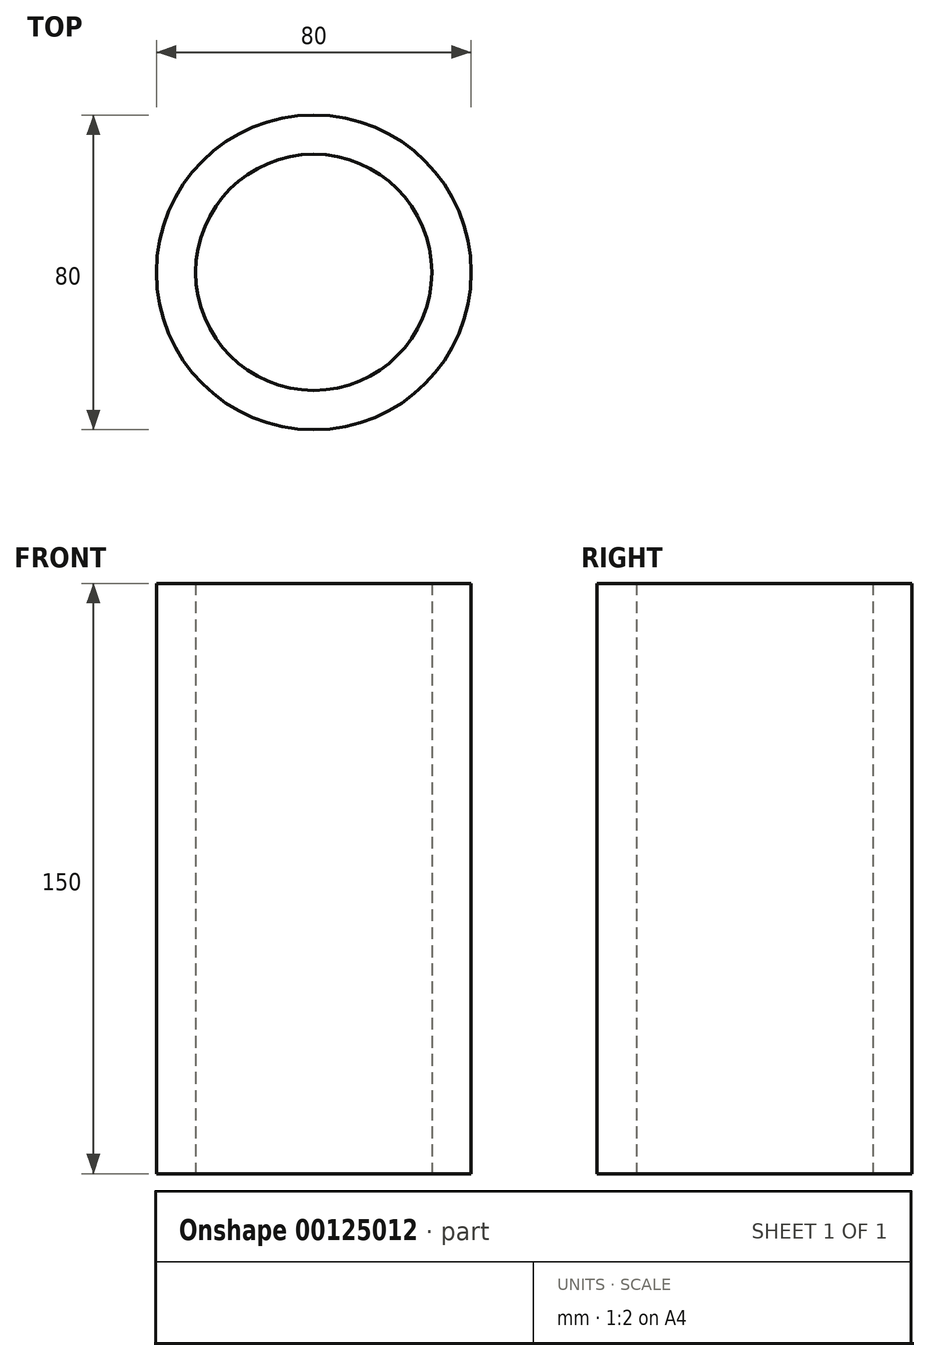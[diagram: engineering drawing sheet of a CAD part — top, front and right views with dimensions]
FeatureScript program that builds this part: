
annotation { "Feature Type Name" : "Feature", "Feature Type Description" : "" }
export const myFeature = defineFeature(function(context is Context, id is Id, definition is map)
    precondition{}
    {
        {
            var Q0;
            Q0=qCreatedBy(makeId("Top.planeOp"),FACE);
            var sketch = newSketch(context, id + "F0", { "sketchPlane" : qUnion([Q0])});
            skCircle(sketch, "E0", {"center": v(0, 0) * mm, "radius": 30 * mm});
            skCircle(sketch, "E1", {"center": v(0, 0) * mm, "radius": 40 * mm});
            skSolve(sketch);
        }
        {
            var Q0;
            Q0=makeQuery(id+"F0.imprint","IMPRINT",FACE,{"disambiguationData":[TD([[makeQuery(id+"F0.imprint","IMPRINT",EDGE,{"derivedFrom":sQuery(id+"F0.wireOp",EDGE,"E0")}),-1.0]])]});
            extrude(context, id + "F1", {"entities" : qUnion([Q0]), "depth" : 150 * mm});
        }
    });
